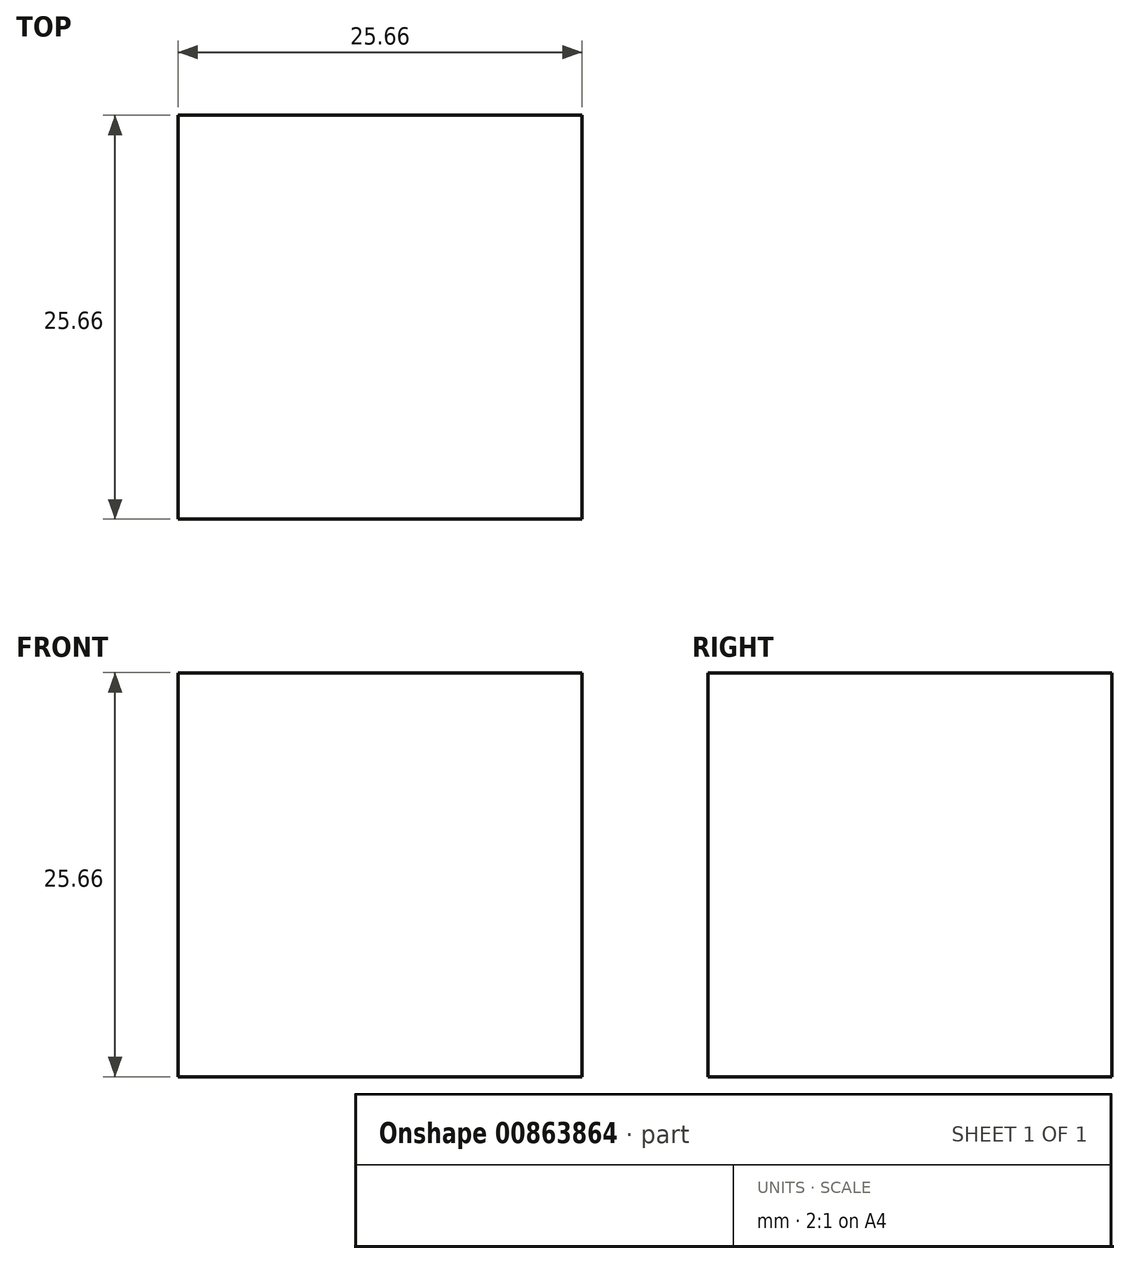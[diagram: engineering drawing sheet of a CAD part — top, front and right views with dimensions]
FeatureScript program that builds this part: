
annotation { "Feature Type Name" : "Feature", "Feature Type Description" : "" }
export const myFeature = defineFeature(function(context is Context, id is Id, definition is map)
    precondition{}
    {
        {
            var Q0;
            Q0=qCreatedBy(makeId("Front.planeOp"),FACE);
            var sketch = newSketch(context, id + "F0", { "sketchPlane" : qUnion([Q0])});
            skLineSegment(sketch, "E0.bottom", {"start": v(12.83, -12.83) * mm, "end": v(-12.83, -12.83) * mm});
            skLineSegment(sketch, "E0.top", {"start": v(12.83, 12.83) * mm, "end": v(-12.83, 12.83) * mm});
            skLineSegment(sketch, "E0.left", {"start": v(12.83, -12.83) * mm, "end": v(12.83, 12.83) * mm});
            skLineSegment(sketch, "E0.right", {"start": v(-12.83, -12.83) * mm, "end": v(-12.83, 12.83) * mm});
            skPoint(sketch, "E0.middle", {"position": v(0, 0) * mm});
            skSolve(sketch);
        }
        {
            var Q0;
            Q0=makeQuery(id+"F0.imprint","IMPRINT",FACE,{"disambiguationData":[TD([[makeQuery(id+"F0.imprint","IMPRINT",EDGE,{"derivedFrom":sQuery(id+"F0.wireOp",EDGE,"E0.bottom")}),-1.0]])]});
            extrude(context, id + "F1", {"entities" : qUnion([Q0]), "endBound" : BoundingType.SYMMETRIC, "depth" : 25.65 * mm, "offsetDistance" : 25.4 * mm});
        }
    });
